# Revit family: Холодильные шкафы со стеклянными дверьми POLAIR Standard без канапе
name_source: partatom
category: Оборудование
units: mm (PartAtom-declared; Revit-internal decimal feet)

## family parameters
Всегда вертикально = Да
Классификация = Нет
На основе рабочей плоскости = Нет
Общий = Нет
При загрузке вырезать с полостями = Нет
Размер круглого соединителя = Использовать диаметр
Тип детали = Нормальный
Точка расчета площади = Нет

## types (4) — shared parameters
1 дверь S = Да
Высота = 1960 мм
Диап. рабочих температур = +1....+10
Допустимая нагрузка на полку, кг = 40
Клапан Шредера = +
Корпус = Да
Подсветка = LED, вертикальная
Расположение агрегата = верхнее
Система электропитания В/Гц = 230/50
Терморегулятор = эл.  блок
Тип оттайки = автомат. с системой исп. конденсата
Тип охлаждения = динамический
Условия окр. среды (темп./вл-сть,%) = до +32/до 60
Хладагент = R134a
zero-valued in all types: Отметка по умолчанию

## per-type parameters (varying)
| type | 2 Корпус | 2 дверь S | Вес брутто, кг | Вес нетто, кг | Габаритные размеры, мм | Глубина | Замок | Кол-во полок | Объем, л. | Потребляемая мощность, Вт, не более | Размер полки, мм | Размеры в упаковке, мм | Расход электроэнергии за сутки, кВт/ч | Цена, руб. | Ширина |
| DM105-S без канапе | Нет | Нет | 124 | 105 | 697х710х1960 | 710 мм | опция | 4 | 500 | 350 | 595*455 | 790х744х2125 | 4 | 40 990 | 697 мм |
| DM110-S без канапе | Да | Да | 206 | 176 | 1402х710х1960 | 710 мм |  | 8 | 1000 | 550 | 595*455 | 1490х744х2125 | 7 | 61 600 | 1402 мм |
| DM107-S без канапе | Нет | Нет | 124 | 105 | 697х945х1960 | 945 мм | опция | 4 | 500 | 400 | 530*650 | 790х744х2125 | 5.5 | 45 500 | 697 мм |
| DM114-S без канапе | Да | Да | 235 | 205 | 1402х945х1960 | 945 мм |  | 8 | 1400 | 600 | 530*650 | 1490х988х2125 | 8 | 66 700 | 1402 мм |
